# Revit family: talis_single_lever_basin_mixer_80_32040000
name_source: partatom
category: Plumbing Fixtures
revit_build: Autodesk Revit 2015 (Build: 20140606_1530(x64)
units: mm (PartAtom-declared; Revit-internal decimal feet)

## types (1)
- Chrome 000
    BIMobject category = Taps & Mixers
    BOSUseNativeGeometries = 1
    Brand url = http://www.hansgrohe-int.com
    Default Elevation = 4' - 0"
    Design country = Germany
    EAN code = https://4011097512259
    Edition number = 1
    IFC Classification = Sanitary Terminal
    Installation instructions = https://pro.hansgrohe-int.com
    Manufacturer country = Germany
    Manufacturer name = Hansgrohe
    Masterformat 2014 Code = 01 52 19
    Masterformat 2014 Description = Sanitary Facilities
    Material main = Chrome
    NBS Reference Code = 35-06-82
    NBS Reference Description = Shower Mixers
    Nominal height = 0
    Nominal width = 0
    OmniClass Code = 23-31 11 00
    OmniClass Description = Faucets
    Product Guid = 720ad0c4-4ead-4c9b-ac11-c3c5b93aa4a5
    Product SKU = 32040000
    Product data url = https://bimobject.com
    Product family = Talis
    Product group = Basin mixers
    Product url = https://pro.hansgrohe-int.com
    QR code = http://bimobject.com
    Technical description = https://pro.hansgrohe-int.com
    UNSPSC Code = 301815
    Uniclass 1.4 Code = L725111
    Uniclass 1.4 Description = Mixer taps
    Uniclass 2.0 Code = PR-35-06-82
    Uniclass 2.0 Description = Shower Mixers
    Uniclass 2015 Code = Pr_40_20_87
    Uniclass 2015 Name = Taps and water supply outlet fittings
    Uniformat II Code = D2020
    Uniformat II Description = Domestic Water Distribution
    Weight Net (Kg) = 0

## geometry (parser evidence)
native form markers: Sweep x2
no freeform markers — native parametric forms only
